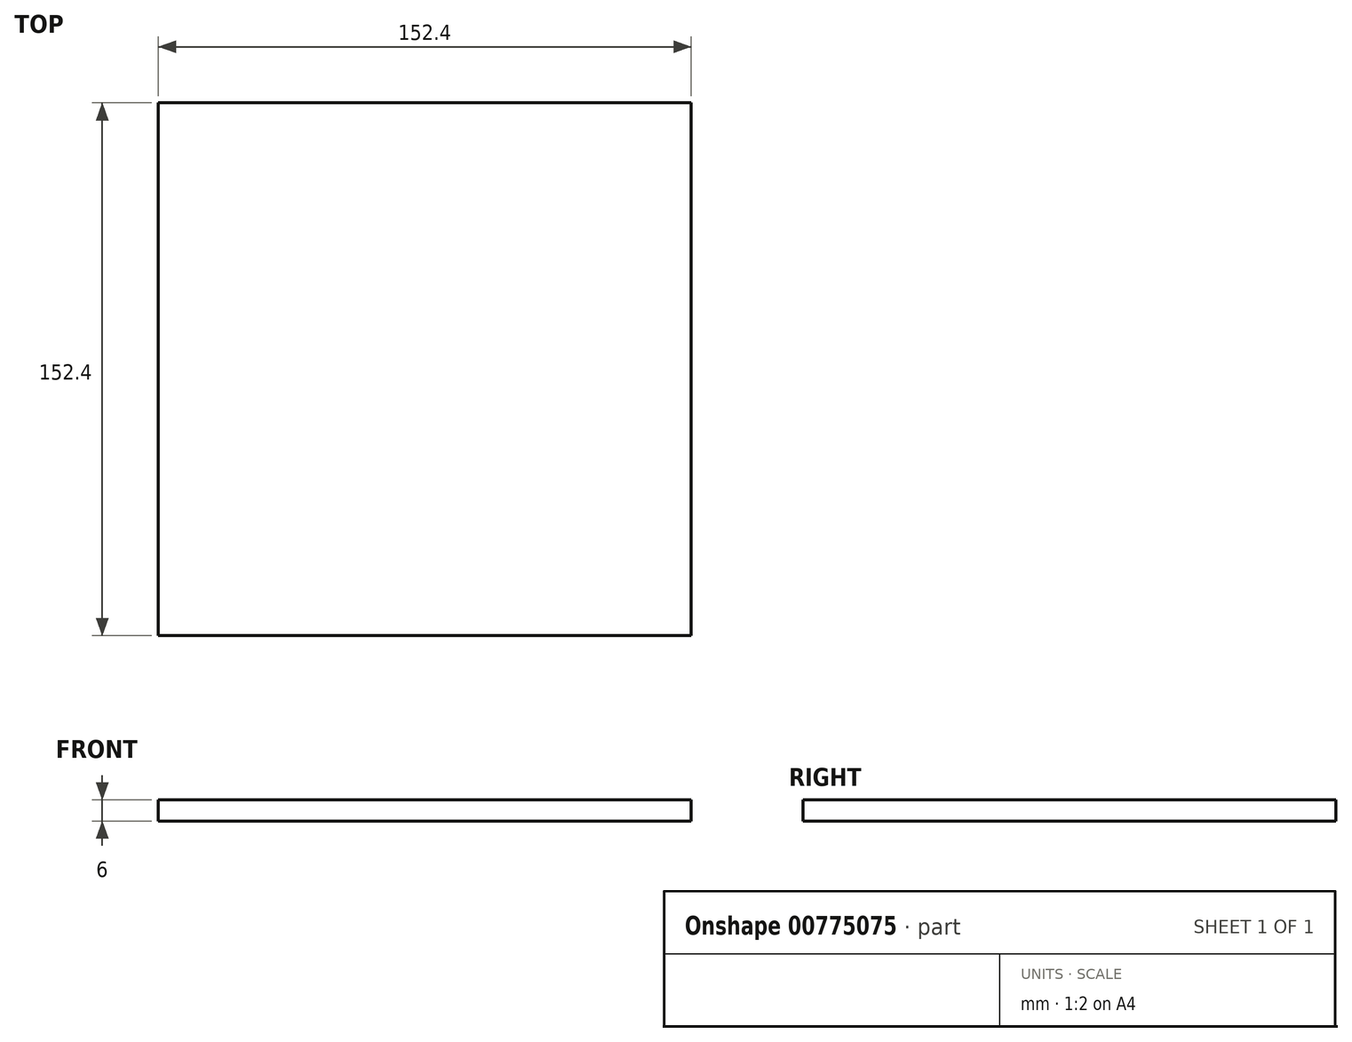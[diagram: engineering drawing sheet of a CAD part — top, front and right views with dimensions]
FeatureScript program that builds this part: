
annotation { "Feature Type Name" : "Feature", "Feature Type Description" : "" }
export const myFeature = defineFeature(function(context is Context, id is Id, definition is map)
    precondition{}
    {
        {
            var Q0;
            Q0=qCreatedBy(makeId("Top.planeOp"),FACE);
            var sketch = newSketch(context, id + "F0", { "sketchPlane" : qUnion([Q0])});
            skLineSegment(sketch, "E0.bottom", {"start": v(76.2, 76.2) * mm, "end": v(-76.2, 76.2) * mm});
            skLineSegment(sketch, "E0.top", {"start": v(76.2, -76.2) * mm, "end": v(-76.2, -76.2) * mm});
            skLineSegment(sketch, "E0.left", {"start": v(76.2, 76.2) * mm, "end": v(76.2, -76.2) * mm});
            skLineSegment(sketch, "E0.right", {"start": v(-76.2, 76.2) * mm, "end": v(-76.2, -76.2) * mm});
            skPoint(sketch, "E0.middle", {"position": v(0, 0) * mm});
            skSolve(sketch);
        }
        {
            var Q0;
            Q0 = qSketchRegion(id + "F0", true);
            extrude(context, id + "F1", {"entities" : qUnion([Q0]), "oppositeDirection" : true, "depth" : 6 * mm, "offsetDistance" : 25.4 * mm});
        }
    });
